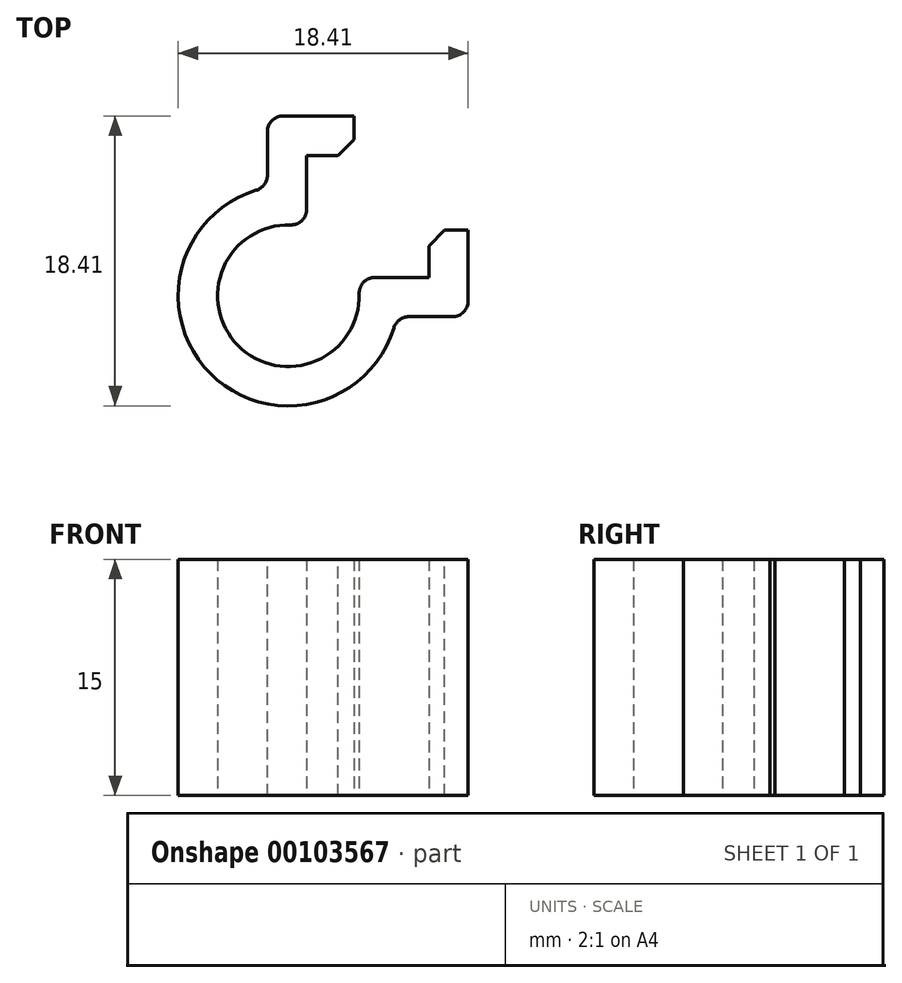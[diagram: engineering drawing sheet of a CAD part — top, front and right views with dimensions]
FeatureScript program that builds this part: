
annotation { "Feature Type Name" : "Feature", "Feature Type Description" : "" }
export const myFeature = defineFeature(function(context is Context, id is Id, definition is map)
    precondition{}
    {
        {
            var Q0;
            Q0=qCreatedBy(makeId("Top.planeOp"),FACE);
            var sketch = newSketch(context, id + "F0", { "sketchPlane" : qUnion([Q0])});
            skLineSegment(sketch, "E0.bottom", {"start": v(0, 0) * mm, "end": v(20, 0) * mm, "construction": true});
            skLineSegment(sketch, "E0.top", {"start": v(0, 20) * mm, "end": v(20, 20) * mm, "construction": true});
            skLineSegment(sketch, "E0.left", {"start": v(0, 0) * mm, "end": v(0, 20) * mm, "construction": true});
            skLineSegment(sketch, "E0.right", {"start": v(20, 0) * mm, "end": v(20, 20) * mm, "construction": true});
            skCircle(sketch, "E1", {"center": v(-1.16, -1.16) * mm, "radius": 4.5 * mm});
            skCircle(sketch, "E2.0", {"center": v(-1.16, -1.16) * mm, "radius": 7 * mm});
            skLineSegment(sketch, "E3", {"start": v(-1.16, -1.16) * mm, "end": v(0, 3.18) * mm, "construction": true});
            skLineSegment(sketch, "E4", {"start": v(-1.16, -1.16) * mm, "end": v(3.18, 0) * mm, "construction": true});
            skLineSegment(sketch, "E5", {"start": v(0, 0) * mm, "end": v(-1.16, -1.16) * mm, "construction": true});
            skLineSegment(sketch, "E6", {"start": v(7.75, 0) * mm, "end": v(7.75, 3) * mm});
            skLineSegment(sketch, "E7", {"start": v(7.75, 3) * mm, "end": v(10.25, 3) * mm});
            skLineSegment(sketch, "E8", {"start": v(10.25, 3) * mm, "end": v(10.25, -2.5) * mm});
            skLineSegment(sketch, "E9", {"start": v(7.75, 0) * mm, "end": v(5.74, 0) * mm});
            skLineSegment(sketch, "E10.MirrorCS", {"start": v(0, 7.75) * mm, "end": v(3, 7.75) * mm});
            skLineSegment(sketch, "E11.MirrorCS", {"start": v(3, 7.75) * mm, "end": v(3, 10.25) * mm});
            skLineSegment(sketch, "E12.MirrorCS", {"start": v(3, 10.25) * mm, "end": v(-2.5, 10.25) * mm});
            skLineSegment(sketch, "E13", {"start": v(0, 7.75) * mm, "end": v(0, 5.74) * mm});
            skLineSegment(sketch, "E14", {"start": v(10.25, -2.5) * mm, "end": v(5.7, -2.5) * mm});
            skLineSegment(sketch, "E15.MirrorCS", {"start": v(-2.5, 10.25) * mm, "end": v(-2.5, 5.7) * mm});
            skLineSegment(sketch, "E16", {"start": v(0, 5.74) * mm, "end": v(0, 3.18) * mm});
            skLineSegment(sketch, "E17", {"start": v(5.74, 0) * mm, "end": v(3.18, 0) * mm});
            skSolve(sketch);
        }
        {
            var Q0;
            Q0=makeQuery(id+"F0.imprint","IMPRINT",FACE,{"disambiguationData":[TD([[makeQuery(id+"F0.imprint","IMPRINT",EDGE,{"derivedFrom":sQuery(id+"F0.wireOp",EDGE,"E10.MirrorCS")}),1.0]])]});
            var Q1;
            {var subQ3=sQuery(id+"F0.wireOp",EDGE,"E16");Q1=makeQuery(id+"F0.imprint","IMPRINT",FACE,{"disambiguationData":[TD([[makeQuery(id+"F0.imprint","IMPRINT",EDGE,{"derivedFrom":subQ3}),-1.0]])]});}
            var Q2;
            Q2=makeQuery(id+"F0.imprint","IMPRINT",FACE,{"disambiguationData":[TD([[makeQuery(id+"F0.imprint","IMPRINT",EDGE,{"derivedFrom":sQuery(id+"F0.wireOp",EDGE,"E6")}),-1.0]])]});
            extrude(context, id + "F1", {"entities" : qUnion([Q0, Q1, Q2]), "depth" : 15 * mm});
        }
        {
            var Q0;
            Q0=makeQuery(id+"F1.opExtrude","SWEPT_EDGE",EDGE,{"disambiguationData":[OSD([sQuery(id+"F0.wireOp",EDGE,"E10.MirrorCS"),sQuery(id+"F0.wireOp",EDGE,"E11.MirrorCS")])]});
            var Q1;
            Q1=makeQuery(id+"F1.opExtrude","SWEPT_EDGE",EDGE,{"disambiguationData":[OSD([sQuery(id+"F0.wireOp",EDGE,"E6"),sQuery(id+"F0.wireOp",EDGE,"E7")])]});
            chamfer(context, id + "F2", {"entities" : qUnion([Q0, Q1]), "width" : 1 * mm, "tangentPropagation" : true});
        }
        {
            var Q0;
            Q0=makeQuery(id+"F1.opExtrude","SWEPT_EDGE",EDGE,{"disambiguationData":[OSD([sQuery(id+"F0.wireOp",EDGE,"E8"),sQuery(id+"F0.wireOp",EDGE,"E14")])]});
            var Q1;
            Q1=makeQuery(id+"F1.opExtrude","SWEPT_EDGE",EDGE,{"disambiguationData":[OSD([sQuery(id+"F0.wireOp",EDGE,"E1"),sQuery(id+"F0.wireOp",EDGE,"E16")])]});
            var Q2;
            Q2=makeQuery(id+"F1.opExtrude","SWEPT_EDGE",EDGE,{"disambiguationData":[OSD([sQuery(id+"F0.wireOp",EDGE,"E12.MirrorCS"),sQuery(id+"F0.wireOp",EDGE,"E15.MirrorCS")])]});
            var Q3;
            Q3=makeQuery(id+"F1.opExtrude","SWEPT_EDGE",EDGE,{"disambiguationData":[OSD([sQuery(id+"F0.wireOp",EDGE,"E1"),sQuery(id+"F0.wireOp",EDGE,"E17")])]});
            var Q4;
            Q4=makeQuery(id+"F1.opExtrude","SWEPT_EDGE",EDGE,{"disambiguationData":[OSD([sQuery(id+"F0.wireOp",EDGE,"E2.0"),sQuery(id+"F0.wireOp",EDGE,"E15.MirrorCS")])]});
            var Q5;
            Q5=makeQuery(id+"F1.opExtrude","SWEPT_EDGE",EDGE,{"disambiguationData":[OSD([sQuery(id+"F0.wireOp",EDGE,"E2.0"),sQuery(id+"F0.wireOp",EDGE,"E14")])]});
            fillet(context, id + "F3", {"entities" : qUnion([Q0, Q1, Q2, Q3, Q4, Q5]), "radius" : 1 * mm, "tangentPropagation" : true, "allowEdgeOverflow" : false});
        }
    });
